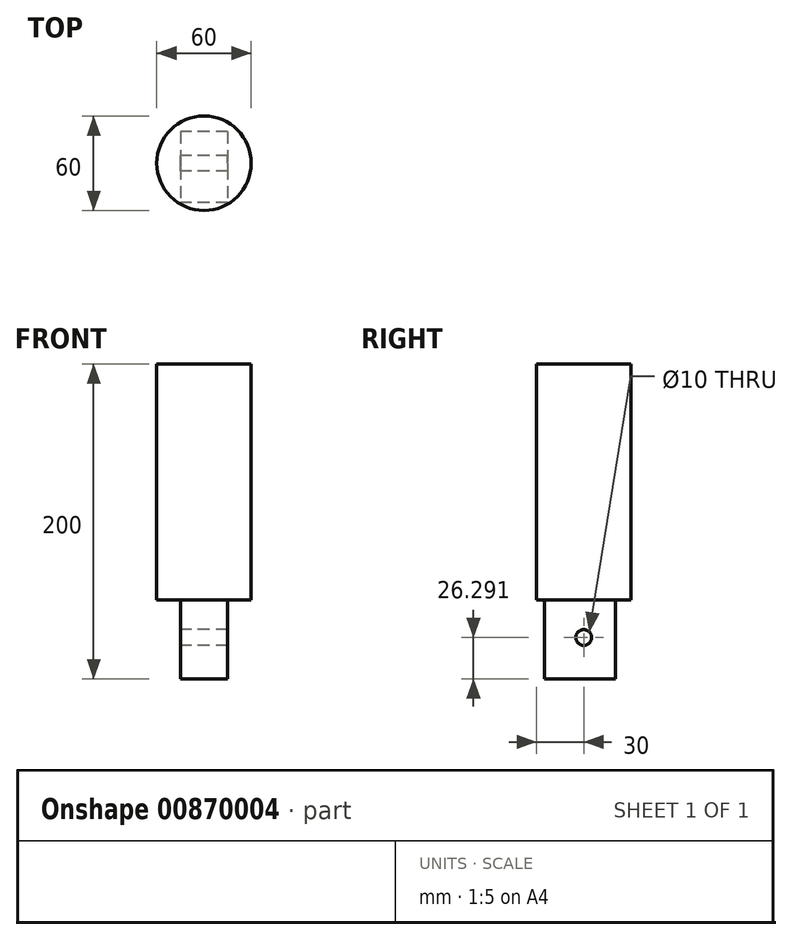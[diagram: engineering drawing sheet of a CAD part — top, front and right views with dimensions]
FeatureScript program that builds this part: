
annotation { "Feature Type Name" : "Feature", "Feature Type Description" : "" }
export const myFeature = defineFeature(function(context is Context, id is Id, definition is map)
    precondition{}
    {
        {
            var Q0;
            Q0=qCreatedBy(makeId("Front.planeOp"),FACE);
            var sketch = newSketch(context, id + "F0", { "sketchPlane" : qUnion([Q0])});
            skLineSegment(sketch, "E0", {"start": v(0, 0) * mm, "end": v(30, 0) * mm});
            skLineSegment(sketch, "E1", {"start": v(30, 0) * mm, "end": v(30, 150) * mm});
            skLineSegment(sketch, "E2", {"start": v(0, 150) * mm, "end": v(30, 150) * mm});
            skLineSegment(sketch, "E3", {"start": v(0, 0) * mm, "end": v(0, 150) * mm});
            skSolve(sketch);
        }
        {
            var Q0;
            Q0 = qSketchRegion(id + "F0", true);
            var Q1;
            Q1=sQuery(id+"F0.wireOp",EDGE,"E3");
            revolve(context, id + "F1", {"surfaceOperationType" : NewSurfaceOperationType.NEW, "entities" : qUnion([Q0]), "axis" : qUnion([Q1]), "revolveType" : RevolveType.FULL});
        }
        {
            var Q0;
            Q0=qCreatedBy(makeId("Front.planeOp"),FACE);
            var sketch = newSketch(context, id + "F2", { "sketchPlane" : qUnion([Q0])});
            skLineSegment(sketch, "E4.bottom", {"start": v(15, -50) * mm, "end": v(-15, -50) * mm});
            skLineSegment(sketch, "E4.top", {"start": v(15, 50) * mm, "end": v(-15, 50) * mm});
            skLineSegment(sketch, "E4.left", {"start": v(15, -50) * mm, "end": v(15, 50) * mm});
            skLineSegment(sketch, "E4.right", {"start": v(-15, -50) * mm, "end": v(-15, 50) * mm});
            skPoint(sketch, "E4.middle", {"position": v(0, 0) * mm});
            skSolve(sketch);
        }
        {
            var Q0;
            Q0 = qSketchRegion(id + "F2", true);
            extrude(context, id + "F3", {"entities" : qUnion([Q0]), "operationType" : NewBodyOperationType.ADD, "oppositeDirection" : true, "depth" : 20 * mm, "offsetDistance" : 25 * mm, "hasSecondDirection" : true, "secondDirectionOppositeDirection" : false, "secondDirectionDepth" : 25 * mm});
        }
        {
            var Q0;
            Q0=makeQuery(id+"F3.opExtrude","SWEPT_FACE",FACE,{"disambiguationData":[OSD([sQuery(id+"F2.wireOp",EDGE,"E4.right")])]});
            var sketch = newSketch(context, id + "F4", { "sketchPlane" : qUnion([Q0])});
            skCircle(sketch, "E5", {"center": v(0, -23.7) * mm, "radius": 14.69 * mm});
            skSolve(sketch);
        }
        {
            var Q0;
            Q0=sQuery(id+"F4.wireOp",VERTEX,"E5.center");
            var Q1;
            Q1=makeQuery(id+"F1.opRevolve","SWEPT_BODY",BODY,{"disambiguationData":[OSD([sQuery(id+"F0.wireOp",EDGE,"E0"),sQuery(id+"F0.wireOp",EDGE,"E1"),sQuery(id+"F0.wireOp",EDGE,"E2"),sQuery(id+"F0.wireOp",EDGE,"E3")])]});
            hole(context, id + "F5", {"style" : HoleStyle.SIMPLE, "endStyle" : HoleEndStyle.THROUGH, "holeDiameter" : 10 * mm, "majorDiameter" : 5 * mm, "isTappedThrough" : true, "tappedDepth" : 12 * mm, "tapClearance" : 3, "locations" : qUnion([Q0]), "scope" : qUnion([Q1])});
        }
    });
